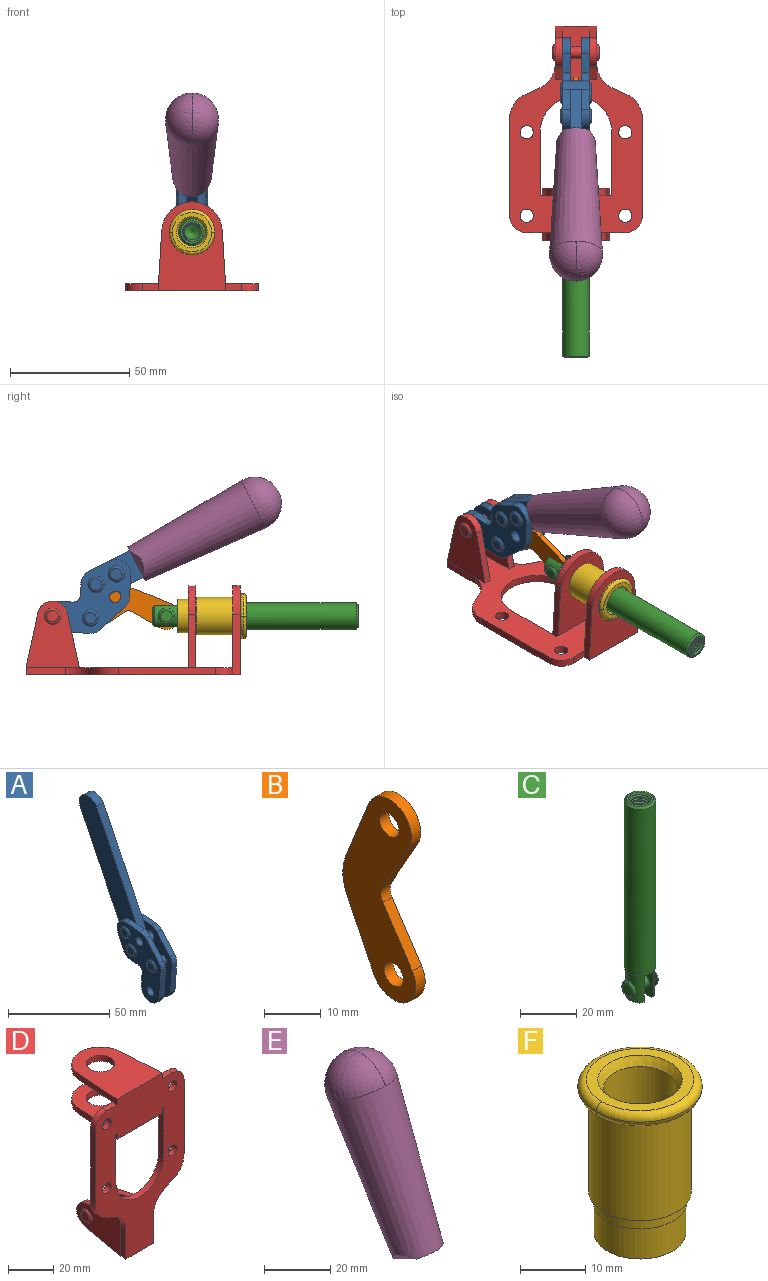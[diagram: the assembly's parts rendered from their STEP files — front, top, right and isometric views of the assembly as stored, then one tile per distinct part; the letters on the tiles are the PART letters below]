
ASSEMBLY  parts=6 mates=6
PART A: 59 faces, bbox 12.9x60.2x99.6 mm
  f0: torus R=2.39mm, axis (-1,0,0), area 14.9mm2, adj f20,f43,f51
  f1: torus R=2.39mm, axis (-1,0,0), area 14.9mm2, adj f19,f42,f51
  f2: torus R=2.39mm, axis (-1,0,0), area 14.9mm2, adj f18,f35,f51
  f3: torus R=2.39mm, axis (-1,0,0), area 14.9mm2, adj f14,f17,f23
  f4: torus R=2.39mm, axis (-1,0,0), area 14.9mm2, adj f13,f16,f23
  f5: torus R=2.39mm, axis (-1,0,0), area 14.9mm2, adj f12,f15,f23
  f6: cylinder r=2.39mm len=4.78mm, axis (1,0,0), area 46.5mm2, adj f48,f50,f51
  f7: cylinder r=2.39mm len=4.78mm, axis (1,0,0), area 46.5mm2, adj f50,f51
  f8: cylinder r=6.35mm len=12.68mm, axis (1,0,0), area 61.8mm2, adj f38,f39,f50,f51
  f9: cylinder r=2.39mm len=4.78mm, axis (-1,0,0), area 70.5mm2, adj f46,f50
  f10: cylinder r=2.39mm len=4.78mm, axis (-1,0,0), area 46.5mm2, adj f23,f45,f46
  f11: cylinder r=2.39mm len=4.78mm, axis (-1,0,0), area 46.5mm2, adj f23,f46
  f12: plane 4.78x4.78mm, normal (1,0,0), area 17.9mm2, adj f5,f15
  f13: plane 4.78x4.78mm, normal (1,0,0), area 17.9mm2, adj f4,f16
  f14: plane 4.78x4.78mm, normal (1,0,0), area 17.9mm2, adj f3,f17
  f15: torus R=2.39mm, axis (-1,0,0), area 14.9mm2, adj f5,f12,f23
  f16: torus R=2.39mm, axis (-1,0,0), area 14.9mm2, adj f4,f13,f23
  f17: torus R=2.39mm, axis (-1,0,0), area 14.9mm2, adj f3,f14,f23
  f18: plane 4.78x4.78mm, normal (-1,0,0), area 17.9mm2, adj f2,f35
  f19: plane 4.78x4.78mm, normal (-1,0,0), area 17.9mm2, adj f1,f42
  f20: plane 4.78x4.78mm, normal (-1,0,0), area 17.9mm2, adj f0,f43
  f21: plane 2.26x0.2mm, normal (1,0,0), area 0.2mm2, adj f31,f44
  f22: plane 2.26x0.2mm, normal (-1,0,0), area 0.2mm2, adj f41,f44
  f23: plane 39.37x30.77mm, normal (1,0,0), area 565.5mm2, adj f3,f4,f5,f10,f11,f15,f16,f17
  f24: cylinder r=6.1mm len=4.15mm, axis (-1,0,0), area 14.7mm2, adj f23,f25,f32,f46
  f25: plane 10.25x9.01mm, normal (0,-0.75,0.66), area 42.3mm2, adj f23,f24,f26,f46
  f26: cylinder r=6.35mm len=4.64mm, axis (-1,0,0), area 15.6mm2, adj f23,f25,f27,f46
  f27: plane 15.84x3.1mm, normal (0,-1,-0.07), area 49.2mm2, adj f23,f26,f28,f46
  f28: cylinder r=6.35mm len=12.68mm, axis (-1,0,0), area 61.8mm2, adj f23,f27,f29,f46
  f29: plane 8.11x3.1mm, normal (0,1,0.07), area 25.2mm2, adj f23,f28,f30,f46
  f30: cylinder r=3.05mm len=3.25mm, axis (-1,0,0), area 14.8mm2, adj f23,f29,f31,f46
  f31: plane 5.99x3.1mm, normal (0,0.07,-1), area 18.6mm2, adj f21,f23,f30,f44,f46
  f32: plane 9.5x3.1mm, normal (0,-0.07,1), area 29.5mm2, adj f23,f24,f33,f46,f47
  f33: cylinder r=6.1mm len=8.63mm, axis (-1,0,0), area 39.1mm2, adj f23,f32,f34,f47
  f34: plane 8.65x3.96mm, normal (0,0.91,-0.42), area 29.5mm2, adj f23,f33,f44,f47
  f35: torus R=2.39mm, axis (-1,0,0), area 14.9mm2, adj f2,f18,f51
  f36: plane 10.25x9.01mm, normal (0,-0.75,0.66), area 42.3mm2, adj f37,f49,f50,f51
  f37: cylinder r=6.35mm len=4.64mm, axis (1,0,0), area 15.6mm2, adj f36,f38,f50,f51
  f38: plane 15.84x3.1mm, normal (0,-1,-0.07), area 49.2mm2, adj f8,f37,f50,f51
  f39: plane 8.11x3.1mm, normal (0,1,0.07), area 25.2mm2, adj f8,f40,f50,f51
  f40: cylinder r=3.05mm len=3.25mm, axis (1,0,0), area 14.8mm2, adj f39,f41,f50,f51
  f41: plane 5.99x3.1mm, normal (0,0.07,-1), area 18.6mm2, adj f22,f40,f44,f50,f51
  f42: torus R=2.39mm, axis (-1,0,0), area 14.9mm2, adj f1,f19,f51
  f43: torus R=2.39mm, axis (-1,0,0), area 14.9mm2, adj f0,f20,f51
  f44: cylinder r=6.35mm len=12.12mm, axis (-1,0,0), area 128.9mm2, adj f21,f22,f23,f31,f34,f41,f46,f47
  f45: plane 2.65x1.35mm, normal (1,0,0), area 1mm2, adj f10,f55
  f46: plane 39.08x20.42mm, normal (-1,0,0), area 412.5mm2, adj f9,f10,f11,f24,f25,f26,f27,f28
  f47: plane 77.62x39.82mm, normal (1,0,0), area 850mm2, adj f32,f33,f34,f44,f53,f54,f55
  f48: plane 2.65x1.35mm, normal (-1,0,0), area 1mm2, adj f6,f55
  f49: cylinder r=6.1mm len=4.15mm, axis (1,0,0), area 14.7mm2, adj f36,f50,f51,f56
  f50: plane 39.08x20.42mm, normal (1,0,0), area 412.5mm2, adj f6,f7,f8,f9,f36,f37,f38,f39
  f51: plane 39.37x30.77mm, normal (-1,0,0), area 565.5mm2, adj f0,f1,f2,f6,f7,f8,f35,f36
  f52: plane 8.65x3.96mm, normal (0,0.91,-0.42), area 29.5mm2, adj f44,f51,f57,f58
  f53: plane 68.49x33.4mm, normal (0,0.9,-0.44), area 358.1mm2, adj f44,f47,f54,f58
  f54: cylinder r=6.35mm len=12.06mm, axis (1,0,0), area 93.7mm2, adj f47,f53,f55,f58
  f55: plane 68.49x33.4mm, normal (0,-0.9,0.44), area 358.1mm2, adj f44,f45,f46,f47,f48,f50,f54,f58
  f56: plane 9.5x3.1mm, normal (0,-0.07,1), area 29.5mm2, adj f49,f50,f51,f57,f58
  f57: cylinder r=6.1mm len=8.63mm, axis (1,0,0), area 39.1mm2, adj f51,f52,f56,f58
  f58: plane 77.62x39.82mm, normal (-1,0,0), area 850mm2, adj f44,f52,f53,f54,f55,f56,f57
PART B: 12 faces, bbox 2.3x18.2x42.8 mm
  f0: cylinder r=2.4mm len=4.8mm, axis (1,0,0), area 34.9mm2, adj f4,f11
  f1: cylinder r=10.41mm len=8.47mm, axis (1,0,0), area 20.2mm2, adj f4,f9,f10,f11
  f2: cylinder r=3.05mm len=3.16mm, axis (1,0,0), area 7.7mm2, adj f4,f6,f7,f11
  f3: cylinder r=2.4mm len=4.8mm, axis (1,0,0), area 34.9mm2, adj f4,f11
  f4: plane 42.81x18.23mm, normal (-1,0,0), area 414.1mm2, adj f0,f1,f2,f3,f5,f6,f7,f8
  f5: cylinder r=5.54mm len=10.67mm, axis (1,0,0), area 41.8mm2, adj f4,f6,f10,f11
  f6: plane 11.66x6.53mm, normal (0,-0.87,-0.49), area 30.9mm2, adj f2,f4,f5,f11
  f7: plane 11.17x7.33mm, normal (0,-0.84,0.55), area 30.9mm2, adj f2,f4,f8,f11
  f8: cylinder r=5.54mm len=10.51mm, axis (1,0,0), area 41.8mm2, adj f4,f7,f9,f11
  f9: plane 13.67x6.67mm, normal (0,0.9,-0.44), area 35.1mm2, adj f1,f4,f8,f11
  f10: plane 14.1x5.7mm, normal (0,0.93,0.37), area 35.1mm2, adj f1,f4,f5,f11
  f11: plane 42.81x18.23mm, normal (1,0,0), area 414.1mm2, adj f0,f1,f2,f3,f5,f6,f7,f8
PART C: 48 faces, bbox 12.6x11.1x86.1 mm
  f0: torus R=2.41mm, axis (-1,0,0), area 15mm2, adj f30,f32,f34
  f1: torus R=2.41mm, axis (-1,0,0), area 15mm2, adj f29,f31,f33
  f2: cylinder r=5.54mm len=72.39mm, axis (0,0,1), area 2518.5mm2, adj f3,f4,f42,f43
  f3: cone r=5.54mm half-angle=45deg, axis (0,0,1), area 7.6mm2, adj f2,f5,f41
  f4: cone r=5.54mm half-angle=45deg, axis (0,0,-1), area 34.9mm2, adj f2,f39
  f5: cylinder r=5.08mm len=11.48mm, axis (0,0,1), area 108.3mm2, adj f3,f7,f8,f41
  f6: cylinder r=2.41mm len=4.83mm, axis (-1,0,0), area 71.2mm2, adj f40,f41
  f7: cylinder r=2.41mm len=4.83mm, axis (-1,0,0), area 7.6mm2, adj f5,f34
  f8: cone r=5.08mm half-angle=45deg, axis (0,0,1), area 10.6mm2, adj f5,f37,f41
  f9: cone r=3.98mm half-angle=45deg, axis (0,0,1), area 17.6mm2, adj f27,f39,f45,f46,f47
  f10: cylinder r=2.41mm len=4.83mm, axis (-1,0,0), area 7.6mm2, adj f33,f38
  f11: cylinder r=3.2mm len=6.4mm, axis (0,0,1), area 78.4mm2, adj f12,f28,f44,f45,f47
  f12: cylinder r=3.2mm len=6.4mm, axis (0,0,1), area 10.5mm2, adj f11,f13,f45,f47
  f13: cylinder r=3.2mm len=6.4mm, axis (0,0,1), area 10.5mm2, adj f12,f14,f45,f47
  f14: cylinder r=3.2mm len=6.4mm, axis (0,0,1), area 10.5mm2, adj f13,f15,f45,f47
  f15: cylinder r=3.2mm len=6.4mm, axis (0,0,1), area 10.5mm2, adj f14,f16,f45,f47
  f16: cylinder r=3.2mm len=6.4mm, axis (0,0,1), area 10.5mm2, adj f15,f17,f45,f47
  f17: cylinder r=3.2mm len=6.4mm, axis (0,0,1), area 10.5mm2, adj f16,f18,f45,f47
  f18: cylinder r=3.2mm len=6.4mm, axis (0,0,1), area 10.5mm2, adj f17,f19,f45,f47
  f19: cylinder r=3.2mm len=6.4mm, axis (0,0,1), area 10.5mm2, adj f18,f20,f45,f47
  f20: cylinder r=3.2mm len=6.4mm, axis (0,0,1), area 10.5mm2, adj f19,f21,f45,f47
  f21: cylinder r=3.2mm len=6.4mm, axis (0,0,1), area 10.5mm2, adj f20,f22,f45,f47
  f22: cylinder r=3.2mm len=6.4mm, axis (0,0,1), area 10.5mm2, adj f21,f23,f45,f47
  f23: cylinder r=3.2mm len=6.4mm, axis (0,0,1), area 10.5mm2, adj f22,f24,f45,f47
  f24: cylinder r=3.2mm len=6.4mm, axis (0,0,1), area 10.5mm2, adj f23,f25,f45,f47
  f25: cylinder r=3.2mm len=6.4mm, axis (0,0,1), area 10.5mm2, adj f24,f26,f45,f47
  f26: cylinder r=3.2mm len=6.4mm, axis (0,0,1), area 10.5mm2, adj f25,f27,f45,f47
  f27: cylinder r=3.2mm len=6.4mm, axis (0,0,1), area 7.4mm2, adj f9,f26,f45,f47
  f28: cone r=3.2mm half-angle=60deg, axis (0,0,1), area 37.2mm2, adj f11
  f29: plane 4.83x4.83mm, normal (-1,0,0), area 18.3mm2, adj f1,f31
  f30: plane 4.83x4.83mm, normal (1,0,0), area 18.3mm2, adj f0,f32
  f31: torus R=2.41mm, axis (-1,0,0), area 15mm2, adj f1,f29,f33
  f32: torus R=2.41mm, axis (-1,0,0), area 15mm2, adj f0,f30,f34
  f33: plane 6.83x6.83mm, normal (1,0,0), area 18.3mm2, adj f1,f10,f31
  f34: plane 6.83x6.83mm, normal (-1,0,0), area 18.3mm2, adj f0,f7,f32
  f35: cone r=5.08mm half-angle=45deg, axis (0,0,1), area 10.6mm2, adj f36,f38,f40
  f36: plane 7.25x1.97mm, normal (0,0,-1), area 10mm2, adj f35,f40
  f37: plane 7.25x1.97mm, normal (0,0,-1), area 10mm2, adj f8,f41
  f38: cylinder r=5.08mm len=11.48mm, axis (0,0,1), area 108.3mm2, adj f10,f35,f40,f42
  f39: plane 9.55x9.55mm, normal (0,0,1), area 22mm2, adj f4,f9
  f40: plane 12.76x10.09mm, normal (1,0,0), area 95.7mm2, adj f6,f35,f36,f38,f42,f43
  f41: plane 12.76x10.09mm, normal (-1,0,0), area 95.7mm2, adj f3,f5,f6,f8,f37,f43
  f42: cone r=5.54mm half-angle=45deg, axis (0,0,1), area 7.6mm2, adj f2,f38,f40
  f43: plane 11.07x4.7mm, normal (0,0,-1), area 50.4mm2, adj f2,f40,f41
  f44: plane 0.89x0.62mm, normal (-1,0,0), area 0.3mm2, adj f11,f45,f46,f47
  f45: bspline ~24.8x7.63mm, area 266.6mm2, adj f9,f11,f12,f13,f14,f15,f16,f17
  f46: bspline ~24.87x7.63mm, area 73.6mm2, adj f9,f44,f45,f47
  f47: bspline ~24.98x7.63mm, area 272.5mm2, adj f9,f11,f12,f13,f14,f15,f16,f17
PART D: 55 faces, bbox 55.7x37.4x89.8 mm
  f0: torus R=2.41mm, axis (-1,0,0), area 15mm2, adj f11,f15,f25
  f1: torus R=2.41mm, axis (-1,0,0), area 15mm2, adj f10,f12,f22
  f2: cylinder r=2.78mm len=5.56mm, axis (0,-1,0), area 54.2mm2, adj f30,f54
  f3: cylinder r=14.99mm len=29.97mm, axis (0,-1,0), area 145.9mm2, adj f30,f49,f53,f54
  f4: cylinder r=2.78mm len=5.56mm, axis (0,-1,0), area 54.2mm2, adj f30,f54
  f5: cylinder r=2.78mm len=5.56mm, axis (0,-1,0), area 54.2mm2, adj f30,f54
  f6: cylinder r=2.78mm len=5.56mm, axis (0,-1,0), area 54.2mm2, adj f30,f54
  f7: cylinder r=6.35mm len=12.7mm, axis (0,0,1), area 123.6mm2, adj f27,f51
  f8: cylinder r=6.35mm len=12.7mm, axis (0,0,-1), area 124.7mm2, adj f21,f35
  f9: cylinder r=2.41mm len=11.18mm, axis (-1,0,0), area 169.4mm2, adj f16,f19
  f10: plane 4.83x4.83mm, normal (1,0,0), area 18.3mm2, adj f1,f12
  f11: plane 4.83x4.83mm, normal (-1,0,0), area 18.3mm2, adj f0,f15
  f12: torus R=2.41mm, axis (-1,0,0), area 15mm2, adj f1,f10,f22
  f13: cylinder r=6.35mm len=12.41mm, axis (1,0,0), area 53.4mm2, adj f18,f19,f22,f23
  f14: cylinder r=6.35mm len=12.41mm, axis (-1,0,0), area 53.4mm2, adj f16,f17,f24,f25
  f15: torus R=2.41mm, axis (-1,0,0), area 15mm2, adj f0,f11,f25
  f16: plane 27.86x22.35mm, normal (1,0,0), area 425.4mm2, adj f9,f14,f17,f24,f30
  f17: plane 22.86x4.97mm, normal (0,0.21,0.98), area 72.5mm2, adj f14,f16,f25,f30
  f18: plane 22.86x4.97mm, normal (0,0.21,0.98), area 72.5mm2, adj f13,f19,f22,f30
  f19: plane 27.86x22.35mm, normal (-1,0,0), area 425.4mm2, adj f9,f13,f18,f23,f30
  f20: cylinder r=12.7mm len=25.35mm, axis (0,0,-1), area 119.8mm2, adj f21,f34,f35,f36
  f21: plane 34.21x28.07mm, normal (0,0,-1), area 702.4mm2, adj f8,f20,f30,f34,f36
  f22: plane 27.96x22.45mm, normal (1,0,0), area 407.2mm2, adj f1,f12,f13,f18,f23,f30,f42,f43
  f23: plane 22.86x4.97mm, normal (0,0.21,-0.98), area 72.5mm2, adj f13,f19,f22,f44
  f24: plane 22.86x4.97mm, normal (0,0.21,-0.98), area 72.5mm2, adj f14,f16,f25,f44
  f25: plane 27.86x22.35mm, normal (-1,0,0), area 407.1mm2, adj f0,f14,f15,f17,f24,f30,f45,f46
  f26: plane 3.1x0.95mm, normal (0,0,-1), area 2.7mm2, adj f30,f49,f50,f54
  f27: plane 34.21x28.07mm, normal (0,0,1), area 702.4mm2, adj f7,f28,f30,f50,f52
  f28: cylinder r=12.7mm len=25.35mm, axis (0,0,1), area 118.8mm2, adj f27,f50,f51,f52
  f29: plane 3.1x0.95mm, normal (0,0,-1), area 2.7mm2, adj f30,f52,f53,f54
  f30: plane 86.54x55.63mm, normal (0,1,0), area 2362.9mm2, adj f2,f3,f4,f5,f6,f16,f17,f18
  f31: plane 40.56x3.1mm, normal (-1,0,0), area 125.7mm2, adj f30,f32,f48,f54
  f32: cylinder r=7.11mm len=7.11mm, axis (0,-1,0), area 34.6mm2, adj f30,f31,f33,f54
  f33: plane 6.67x3.1mm, normal (0,0,1), area 20.4mm2, adj f30,f32,f34,f54
  f34: plane 25.39x3.13mm, normal (-1,0.06,0), area 79.5mm2, adj f20,f21,f33,f35,f54
  f35: plane 37.31x28.45mm, normal (0,0,1), area 789.9mm2, adj f8,f20,f34,f36,f54
  f36: plane 25.39x3.13mm, normal (1,0.06,0), area 79.5mm2, adj f20,f21,f35,f37,f54
  f37: plane 6.67x3.1mm, normal (0,0,1), area 20.4mm2, adj f30,f36,f38,f54
  f38: cylinder r=7.11mm len=7.11mm, axis (0,-1,0), area 34.6mm2, adj f30,f37,f39,f54
  f39: plane 40.56x3.1mm, normal (1,0,0), area 125.7mm2, adj f30,f38,f40,f54
  f40: cylinder r=11.18mm len=10.16mm, axis (0,-1,0), area 39.5mm2, adj f30,f39,f41,f54
  f41: plane 6.09x3.1mm, normal (0.42,0,-0.91), area 20.8mm2, adj f30,f40,f42,f54
  f42: cylinder r=11.18mm len=9.41mm, axis (0,-1,0), area 37.2mm2, adj f22,f30,f41,f43,f54
  f43: plane 16.5x3.1mm, normal (1,0,0), area 51.1mm2, adj f22,f42,f44,f54
  f44: plane 17.37x3.1mm, normal (0,0,-1), area 53.8mm2, adj f23,f24,f30,f43,f45,f54
  f45: plane 16.5x3.1mm, normal (-1,0,0), area 51.1mm2, adj f25,f44,f46,f54
  f46: cylinder r=11.18mm len=9.41mm, axis (0,-1,0), area 37.2mm2, adj f25,f30,f45,f47,f54
  f47: plane 6.09x3.1mm, normal (-0.42,0,-0.91), area 20.8mm2, adj f30,f46,f48,f54
  f48: cylinder r=11.18mm len=10.16mm, axis (0,-1,0), area 39.5mm2, adj f30,f31,f47,f54
  f49: plane 26.54x3.1mm, normal (-1,0,0), area 82.3mm2, adj f3,f26,f30,f54
  f50: plane 25.39x3.1mm, normal (1,0.06,0), area 78.8mm2, adj f26,f27,f28,f51,f54
  f51: plane 37.31x28.45mm, normal (0,0,-1), area 789.9mm2, adj f7,f28,f50,f52,f54
  f52: plane 25.39x3.1mm, normal (-1,0.06,0), area 78.8mm2, adj f27,f28,f29,f51,f54
  f53: plane 26.54x3.1mm, normal (1,0,0), area 82.3mm2, adj f3,f29,f30,f54
  f54: plane 89.66x55.63mm, normal (0,-1,0), area 2678.5mm2, adj f2,f3,f4,f5,f6,f26,f29,f31
PART E: 11 faces, bbox 22.3x42.6x64.5 mm
  f0: sphere r=11.13mm, area 411.4mm2, adj f1,f8
  f1: cone r=11.11mm half-angle=3.3deg, axis (0,0.44,0.9), area 3251.8mm2, adj f0,f7,f8,f9,f10
  f2: cylinder r=6.16mm len=11.7mm, axis (1,0,0), area 89.5mm2, adj f3,f4,f5,f6
  f3: plane 60.23x36.75mm, normal (-1,0,0), area 763.6mm2, adj f2,f4,f6,f10
  f4: plane 51.37x25.05mm, normal (0,0.9,-0.44), area 264.2mm2, adj f2,f3,f5,f10
  f5: plane 60.23x36.75mm, normal (1,0,0), area 763.6mm2, adj f2,f4,f6,f10
  f6: plane 51.37x25.05mm, normal (0,-0.9,0.44), area 264.2mm2, adj f2,f3,f5,f10
  f7: plane 9.95x5.95mm, normal (0.71,-0.31,-0.64), area 25.8mm2, adj f1,f10
  f8: sphere r=11.13mm, area 411.4mm2, adj f0,f1
  f9: plane 9.95x5.95mm, normal (-0.71,-0.31,-0.64), area 25.8mm2, adj f1,f10
  f10: plane 14.27x11.38mm, normal (0,-0.44,-0.9), area 106.7mm2, adj f1,f3,f4,f5,f6,f7,f9
PART F: 15 faces, bbox 20.6x20.6x28.7 mm
  f0: torus R=8.26mm, axis (0,0,1), area 56.8mm2, adj f1,f10,f12
  f1: torus R=8.26mm, axis (0,0,1), area 56.8mm2, adj f0,f6,f13
  f2: cylinder r=5.59mm len=25.91mm, axis (0,0,1), area 909.6mm2, adj f3,f4
  f3: cone r=6.86mm half-angle=45deg, axis (0,0,-1), area 70.2mm2, adj f2,f14
  f4: cone r=6.47mm half-angle=30deg, axis (0,0,1), area 66.7mm2, adj f2,f13
  f5: cylinder r=7.04mm len=14.07mm, axis (0,0,1), area 252.6mm2, adj f11,f14
  f6: torus R=8.26mm, axis (0,0,1), area 56.8mm2, adj f1,f12,f13
  f7: cylinder r=7.16mm len=14.33mm, axis (0,0,1), area 91.5mm2, adj f9,f11
  f8: cylinder r=7.86mm len=18.42mm, axis (0,0,1), area 909.6mm2, adj f9,f10
  f9: plane 15.72x15.72mm, normal (0,0,-1), area 33mm2, adj f7,f8
  f10: plane 16.51x16.51mm, normal (0,0,-1), area 19.9mm2, adj f0,f8,f12
  f11: plane 14.33x14.33mm, normal (0,0,-1), area 5.7mm2, adj f5,f7
  f12: torus R=8.26mm, axis (0,0,1), area 56.8mm2, adj f0,f6,f10
  f13: plane 16.51x16.51mm, normal (0,0,1), area 82.7mm2, adj f1,f4,f6
  f14: plane 14.07x14.07mm, normal (0,0,-1), area 7.8mm2, adj f3,f5
PLACE A rot(axis=(1,0,0),89deg) t=(0,9.02,0.54)mm
PLACE B rot(axis=(1,0,0),90.5deg) t=(0,9.61,0.13)mm
PLACE C rot(axis=(1,0,0),90deg) t=(0,9.41,0)mm
PLACE D rot(axis=(1,0,0),90deg) t=(0,9.43,0)mm fixed
PLACE E rot(axis=(1,0,0),89deg) t=(0,9.02,0.54)mm
PLACE F rot(axis=(1,0,0),90deg) t=(0,9.43,0)mm
MATE slider C.f2 <-> D.f7  axis (0,-1,0) through (0,-49.38,24.61)mm
MATE revolute C.f6 <-> B.f5  axis (-1,0,0) through (0,-6.07,24.61)mm
MATE fastened F.f0 <-> D.f7  axis (0,1,0) through (0,-36.96,24.61)mm
MATE revolute B.f3 <-> A.f4  axis (1,0,0) through (0,25.67,23.77)mm
MATE revolute A.f7 <-> D.f0  axis (-1,0,0) through (0,41.52,24.61)mm
MATE fastened A.f54 <-> E.f2  axis (1,0,0) through (0,-44.55,72.5)mm
